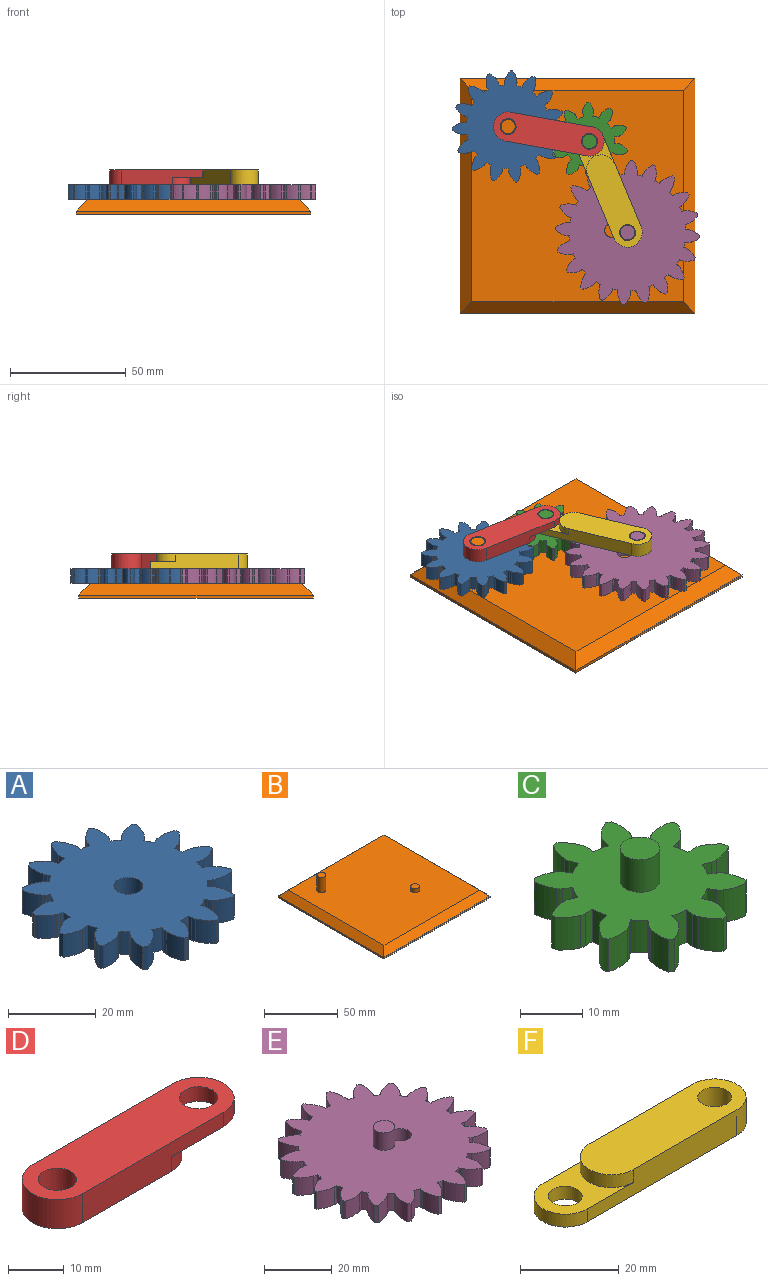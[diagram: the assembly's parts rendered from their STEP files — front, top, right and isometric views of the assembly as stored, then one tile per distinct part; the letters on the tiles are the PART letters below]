
ASSEMBLY  parts=6 mates=6
PART A: 123 faces, bbox 48.3x48.1x6.4 mm
  f0: plane 48.35x48.08mm, normal (0,0,1), area 1375mm2, adj f1,f2,f3,f4,f5,f6,f7,f9
  f1: plane 6.35x0.77mm, normal (-0.96,0.29,0), area 5.1mm2, adj f0,f7,f8,f9
  f2: plane 6.35x0.69mm, normal (0.86,-0.52,0), area 5.1mm2, adj f0,f3,f8,f25
  f3: cylinder r=4.25mm len=6.35mm, axis (0,0,-1), area 6.7mm2, adj f0,f2,f4,f8
  f4: cylinder r=9.71mm len=6.35mm, axis (0,0,-1), area 31.8mm2, adj f0,f3,f5,f8
  f5: plane 6.35x0.91mm, normal (0.41,0.91,0), area 6.3mm2, adj f0,f4,f6,f8
  f6: cylinder r=9.71mm len=6.35mm, axis (0,0,-1), area 31.8mm2, adj f0,f5,f7,f8
  f7: cylinder r=4.25mm len=6.35mm, axis (0,0,-1), area 6.7mm2, adj f0,f1,f6,f8
  f8: plane 48.35x48.08mm, normal (0,0,-1), area 1375mm2, adj f1,f2,f3,f4,f5,f6,f7,f9
  f9: cylinder r=18.11mm len=6.35mm, axis (0,0,-1), area 15.9mm2, adj f0,f1,f8,f117
  f10: plane 6.35x0.8mm, normal (-0.02,1,0), area 5.1mm2, adj f0,f8,f16,f17
  f11: plane 6.35x0.78mm, normal (-0.23,-0.97,0), area 5.1mm2, adj f0,f8,f12,f34
  f12: cylinder r=4.25mm len=6.35mm, axis (0,0,-1), area 6.7mm2, adj f0,f8,f11,f13
  f13: cylinder r=9.71mm len=6.35mm, axis (0,0,-1), area 31.8mm2, adj f0,f8,f12,f14
  f14: plane 6.35x0.99mm, normal (0.99,-0.1,0), area 6.3mm2, adj f0,f8,f13,f15
  f15: cylinder r=9.71mm len=6.35mm, axis (0,0,-1), area 31.8mm2, adj f0,f8,f14,f16
  f16: cylinder r=4.25mm len=6.35mm, axis (0,0,-1), area 6.7mm2, adj f0,f8,f10,f15
  f17: cylinder r=18.11mm len=6.35mm, axis (0,0,-1), area 15.9mm2, adj f0,f8,f10,f27
  f18: plane 6.35x0.61mm, normal (-0.76,0.65,0), area 5.1mm2, adj f0,f8,f24,f25
  f19: plane 6.35x0.66mm, normal (0.57,-0.82,0), area 5.1mm2, adj f0,f8,f20,f33
  f20: cylinder r=4.25mm len=6.35mm, axis (0,0,-1), area 6.7mm2, adj f0,f8,f19,f21
  f21: cylinder r=9.71mm len=6.35mm, axis (0,0,-1), area 31.8mm2, adj f0,f8,f20,f22
  f22: plane 6.35x0.74mm, normal (0.74,0.67,0), area 6.3mm2, adj f0,f8,f21,f23
  f23: cylinder r=9.71mm len=6.35mm, axis (0,0,-1), area 31.8mm2, adj f0,f8,f22,f24
  f24: cylinder r=4.25mm len=6.35mm, axis (0,0,-1), area 6.7mm2, adj f0,f8,f18,f23
  f25: cylinder r=18.11mm len=6.35mm, axis (0,0,-1), area 15.9mm2, adj f0,f2,f8,f18
  f26: plane 6.35x0.73mm, normal (-0.42,0.91,0), area 5.1mm2, adj f0,f8,f32,f33
  f27: plane 6.35x0.79mm, normal (0.19,-0.98,0), area 5.1mm2, adj f0,f8,f17,f28
  f28: cylinder r=4.25mm len=6.35mm, axis (0,0,-1), area 6.7mm2, adj f0,f8,f27,f29
  f29: cylinder r=9.71mm len=6.35mm, axis (0,0,-1), area 31.8mm2, adj f0,f8,f28,f30
  f30: plane 6.35x0.95mm, normal (0.95,0.31,0), area 6.3mm2, adj f0,f8,f29,f31
  f31: cylinder r=9.71mm len=6.35mm, axis (0,0,-1), area 31.8mm2, adj f0,f8,f30,f32
  f32: cylinder r=4.25mm len=6.35mm, axis (0,0,-1), area 6.7mm2, adj f0,f8,f26,f31
  f33: cylinder r=18.11mm len=6.35mm, axis (0,0,-1), area 15.9mm2, adj f0,f8,f19,f26
  f34: cylinder r=18.11mm len=6.35mm, axis (0,0,-1), area 15.9mm2, adj f0,f8,f11,f95
  f35: cylinder r=18.11mm len=6.35mm, axis (0,0,-1), area 15.9mm2, adj f0,f8,f110,f116
  f36: cylinder r=18.11mm len=6.35mm, axis (0,0,-1), area 15.9mm2, adj f0,f8,f103,f109
  f37: cylinder r=18.11mm len=6.35mm, axis (0,0,-1), area 15.9mm2, adj f0,f8,f88,f96
  f38: cylinder r=18.11mm len=6.35mm, axis (0,0,-1), area 15.9mm2, adj f0,f8,f81,f89
  f39: cylinder r=18.11mm len=6.35mm, axis (0,0,-1), area 15.9mm2, adj f0,f8,f74,f82
  f40: cylinder r=18.11mm len=6.35mm, axis (0,0,-1), area 15.9mm2, adj f0,f8,f67,f75
  f41: cylinder r=18.11mm len=6.35mm, axis (0,0,-1), area 15.9mm2, adj f0,f8,f60,f68
  f42: cylinder r=18.11mm len=6.35mm, axis (0,0,-1), area 15.9mm2, adj f0,f8,f53,f61
  f43: cylinder r=18.11mm len=6.35mm, axis (0,0,-1), area 15.9mm2, adj f0,f8,f46,f54
  f44: cylinder r=18.11mm len=6.35mm, axis (0,0,-1), area 15.9mm2, adj f0,f8,f47,f102
  f45: cylinder r=3.3mm len=6.6mm, axis (0,0,-1), area 131.7mm2, adj f0,f8
  f46: plane 6.35x0.79mm, normal (-0.19,-0.98,0), area 5.1mm2, adj f0,f8,f43,f52
  f47: plane 6.35x0.73mm, normal (0.42,0.91,0), area 5.1mm2, adj f0,f8,f44,f48
  f48: cylinder r=4.25mm len=6.35mm, axis (0,0,-1), area 6.7mm2, adj f0,f8,f47,f49
  f49: cylinder r=9.71mm len=6.35mm, axis (0,0,-1), area 31.8mm2, adj f0,f8,f48,f50
  f50: plane 6.35x0.95mm, normal (-0.95,0.31,0), area 6.3mm2, adj f0,f8,f49,f51
  f51: cylinder r=9.71mm len=6.35mm, axis (0,0,-1), area 31.8mm2, adj f0,f8,f50,f52
  f52: cylinder r=4.25mm len=6.35mm, axis (0,0,-1), area 6.7mm2, adj f0,f8,f46,f51
  f53: plane 6.35x0.78mm, normal (0.23,-0.97,0), area 5.1mm2, adj f0,f8,f42,f59
  f54: plane 6.35x0.8mm, normal (0.02,1,0), area 5.1mm2, adj f0,f8,f43,f55
  f55: cylinder r=4.25mm len=6.35mm, axis (0,0,-1), area 6.7mm2, adj f0,f8,f54,f56
  f56: cylinder r=9.71mm len=6.35mm, axis (0,0,-1), area 31.8mm2, adj f0,f8,f55,f57
  f57: plane 6.35x0.99mm, normal (-0.99,-0.1,0), area 6.3mm2, adj f0,f8,f56,f58
  f58: cylinder r=9.71mm len=6.35mm, axis (0,0,-1), area 31.8mm2, adj f0,f8,f57,f59
  f59: cylinder r=4.25mm len=6.35mm, axis (0,0,-1), area 6.7mm2, adj f0,f8,f53,f58
  f60: plane 6.35x0.64mm, normal (0.6,-0.8,0), area 5.1mm2, adj f0,f8,f41,f66
  f61: plane 6.35x0.74mm, normal (-0.39,0.92,0), area 5.1mm2, adj f0,f8,f42,f62
  f62: cylinder r=4.25mm len=6.35mm, axis (0,0,-1), area 6.7mm2, adj f0,f8,f61,f63
  f63: cylinder r=9.71mm len=6.35mm, axis (0,0,-1), area 31.8mm2, adj f0,f8,f62,f64
  f64: plane 6.35x0.87mm, normal (-0.87,-0.5,0), area 6.3mm2, adj f0,f8,f63,f65
  f65: cylinder r=9.71mm len=6.35mm, axis (0,0,-1), area 31.8mm2, adj f0,f8,f64,f66
  f66: cylinder r=4.25mm len=6.35mm, axis (0,0,-1), area 6.7mm2, adj f0,f8,f60,f65
  f67: plane 6.35x0.71mm, normal (0.88,-0.48,0), area 5.1mm2, adj f0,f8,f40,f73
  f68: plane 6.35x0.59mm, normal (-0.73,0.68,0), area 5.1mm2, adj f0,f8,f41,f69
  f69: cylinder r=4.25mm len=6.35mm, axis (0,0,-1), area 6.7mm2, adj f0,f8,f68,f70
  f70: cylinder r=9.71mm len=6.35mm, axis (0,0,-1), area 31.8mm2, adj f0,f8,f69,f71
  f71: plane 6.35x0.81mm, normal (-0.59,-0.81,0), area 6.3mm2, adj f0,f8,f70,f72
  f72: cylinder r=9.71mm len=6.35mm, axis (0,0,-1), area 31.8mm2, adj f0,f8,f71,f73
  f73: cylinder r=4.25mm len=6.35mm, axis (0,0,-1), area 6.7mm2, adj f0,f8,f67,f72
  f74: plane 6.35x0.8mm, normal (1,-0.09,0), area 5.1mm2, adj f0,f8,f39,f80
  f75: plane 6.35x0.76mm, normal (-0.94,0.33,0), area 5.1mm2, adj f0,f8,f40,f76
  f76: cylinder r=4.25mm len=6.35mm, axis (0,0,-1), area 6.7mm2, adj f0,f8,f75,f77
  f77: cylinder r=9.71mm len=6.35mm, axis (0,0,-1), area 31.8mm2, adj f0,f8,f76,f78
  f78: plane 6.35x0.98mm, normal (-0.21,-0.98,0), area 6.3mm2, adj f0,f8,f77,f79
  f79: cylinder r=9.71mm len=6.35mm, axis (0,0,-1), area 31.8mm2, adj f0,f8,f78,f80
  f80: cylinder r=4.25mm len=6.35mm, axis (0,0,-1), area 6.7mm2, adj f0,f8,f74,f79
  f81: plane 6.35x0.76mm, normal (0.94,0.33,0), area 5.1mm2, adj f0,f8,f38,f87
  f82: plane 6.35x0.8mm, normal (-1,-0.09,0), area 5.1mm2, adj f0,f8,f39,f83
  f83: cylinder r=4.25mm len=6.35mm, axis (0,0,-1), area 6.7mm2, adj f0,f8,f82,f84
  f84: cylinder r=9.71mm len=6.35mm, axis (0,0,-1), area 31.8mm2, adj f0,f8,f83,f85
  f85: plane 6.35x0.98mm, normal (0.21,-0.98,0), area 6.3mm2, adj f0,f8,f84,f86
  f86: cylinder r=9.71mm len=6.35mm, axis (0,0,-1), area 31.8mm2, adj f0,f8,f85,f87
  f87: cylinder r=4.25mm len=6.35mm, axis (0,0,-1), area 6.7mm2, adj f0,f8,f81,f86
  f88: plane 6.35x0.59mm, normal (0.73,0.68,0), area 5.1mm2, adj f0,f8,f37,f94
  f89: plane 6.35x0.71mm, normal (-0.88,-0.48,0), area 5.1mm2, adj f0,f8,f38,f90
  f90: cylinder r=4.25mm len=6.35mm, axis (0,0,-1), area 6.7mm2, adj f0,f8,f89,f91
  f91: cylinder r=9.71mm len=6.35mm, axis (0,0,-1), area 31.8mm2, adj f0,f8,f90,f92
  f92: plane 6.35x0.81mm, normal (0.59,-0.81,0), area 6.3mm2, adj f0,f8,f91,f93
  f93: cylinder r=9.71mm len=6.35mm, axis (0,0,-1), area 31.8mm2, adj f0,f8,f92,f94
  f94: cylinder r=4.25mm len=6.35mm, axis (0,0,-1), area 6.7mm2, adj f0,f8,f88,f93
  f95: plane 6.35x0.74mm, normal (0.39,0.92,0), area 5.1mm2, adj f0,f8,f34,f101
  f96: plane 6.35x0.64mm, normal (-0.6,-0.8,0), area 5.1mm2, adj f0,f8,f37,f97
  f97: cylinder r=4.25mm len=6.35mm, axis (0,0,-1), area 6.7mm2, adj f0,f8,f96,f98
  f98: cylinder r=9.71mm len=6.35mm, axis (0,0,-1), area 31.8mm2, adj f0,f8,f97,f99
  f99: plane 6.35x0.87mm, normal (0.87,-0.5,0), area 6.3mm2, adj f0,f8,f98,f100
  f100: cylinder r=9.71mm len=6.35mm, axis (0,0,-1), area 31.8mm2, adj f0,f8,f99,f101
  f101: cylinder r=4.25mm len=6.35mm, axis (0,0,-1), area 6.7mm2, adj f0,f8,f95,f100
  f102: plane 6.35x0.66mm, normal (-0.57,-0.82,0), area 5.1mm2, adj f0,f8,f44,f108
  f103: plane 6.35x0.61mm, normal (0.76,0.65,0), area 5.1mm2, adj f0,f8,f36,f104
  f104: cylinder r=4.25mm len=6.35mm, axis (0,0,-1), area 6.7mm2, adj f0,f8,f103,f105
  f105: cylinder r=9.71mm len=6.35mm, axis (0,0,-1), area 31.8mm2, adj f0,f8,f104,f106
  f106: plane 6.35x0.74mm, normal (-0.74,0.67,0), area 6.3mm2, adj f0,f8,f105,f107
  f107: cylinder r=9.71mm len=6.35mm, axis (0,0,-1), area 31.8mm2, adj f0,f8,f106,f108
  f108: cylinder r=4.25mm len=6.35mm, axis (0,0,-1), area 6.7mm2, adj f0,f8,f102,f107
  f109: plane 6.35x0.69mm, normal (-0.86,-0.52,0), area 5.1mm2, adj f0,f8,f36,f115
  f110: plane 6.35x0.77mm, normal (0.96,0.29,0), area 5.1mm2, adj f0,f8,f35,f111
  f111: cylinder r=4.25mm len=6.35mm, axis (0,0,-1), area 6.7mm2, adj f0,f8,f110,f112
  f112: cylinder r=9.71mm len=6.35mm, axis (0,0,-1), area 31.8mm2, adj f0,f8,f111,f113
  f113: plane 6.35x0.91mm, normal (-0.41,0.91,0), area 6.3mm2, adj f0,f8,f112,f114
  f114: cylinder r=9.71mm len=6.35mm, axis (0,0,-1), area 31.8mm2, adj f0,f8,f113,f115
  f115: cylinder r=4.25mm len=6.35mm, axis (0,0,-1), area 6.7mm2, adj f0,f8,f109,f114
  f116: plane 6.35x0.8mm, normal (-0.99,-0.12,0), area 5.1mm2, adj f0,f8,f35,f122
  f117: plane 6.35x0.8mm, normal (0.99,-0.12,0), area 5.1mm2, adj f0,f8,f9,f118
  f118: cylinder r=4.25mm len=6.35mm, axis (0,0,-1), area 6.7mm2, adj f0,f8,f117,f119
  f119: cylinder r=9.71mm len=6.35mm, axis (0,0,-1), area 31.8mm2, adj f0,f8,f118,f120
  f120: plane 6.35x1mm, normal (0,1,0), area 6.3mm2, adj f0,f8,f119,f121
  f121: cylinder r=9.71mm len=6.35mm, axis (0,0,-1), area 31.8mm2, adj f0,f8,f120,f122
  f122: cylinder r=4.25mm len=6.35mm, axis (0,0,-1), area 6.7mm2, adj f0,f8,f116,f121
PART B: 14 faces, bbox 101.6x101.6x19.1 mm
  f0: plane 101.6x1.27mm, normal (0,1,0), area 129mm2, adj f1,f3,f4,f9
  f1: plane 101.6x1.27mm, normal (-1,0,0), area 129mm2, adj f0,f2,f4,f8
  f2: plane 101.6x1.27mm, normal (0,-1,0), area 129mm2, adj f1,f3,f4,f10
  f3: plane 101.6x1.27mm, normal (1,0,0), area 129mm2, adj f0,f2,f4,f11
  f4: plane 101.6x101.6mm, normal (0,0,-1), area 10322.6mm2, adj f0,f1,f2,f3
  f5: plane 91.44x91.44mm, normal (0,0,1), area 8302.9mm2, adj f6,f8,f9,f10,f11,f12
  f6: cylinder r=3.05mm len=6.1mm, axis (0,0,-1), area 60.8mm2, adj f5,f7
  f7: plane 6.1x6.1mm, normal (0,0,1), area 29.2mm2, adj f6
  f8: plane 101.6x5.08mm, normal (-0.71,0,0.71), area 693.4mm2, adj f1,f5,f9,f10
  f9: plane 101.6x5.08mm, normal (0,0.71,0.71), area 693.4mm2, adj f0,f5,f8,f11
  f10: plane 101.6x5.08mm, normal (0,-0.71,0.71), area 693.4mm2, adj f2,f5,f8,f11
  f11: plane 101.6x5.08mm, normal (0.71,0,0.71), area 693.4mm2, adj f3,f5,f9,f10
  f12: cylinder r=3.05mm len=12.7mm, axis (0,0,-1), area 243.2mm2, adj f5,f13
  f13: plane 6.1x6.1mm, normal (0,0,1), area 29.2mm2, adj f12
PART C: 84 faces, bbox 33.6x33.7x12.7 mm
  f0: plane 33.74x33.62mm, normal (0,0,1), area 573.8mm2, adj f1,f2,f3,f4,f6,f7,f8,f9
  f1: cylinder r=2.25mm len=6.35mm, axis (0,0,-1), area 6.5mm2, adj f0,f2,f5,f7
  f2: plane 6.35x1.56mm, normal (0.96,-0.27,0), area 10.3mm2, adj f0,f1,f5,f9
  f3: plane 6.35x1.24mm, normal (-0.77,0.64,0), area 10.3mm2, adj f0,f4,f5,f17
  f4: cylinder r=2.25mm len=6.35mm, axis (0,0,-1), area 6.5mm2, adj f0,f3,f5,f6
  f5: plane 33.74x33.62mm, normal (0,0,-1), area 605.5mm2, adj f1,f2,f3,f4,f6,f7,f8,f9
  f6: cylinder r=8.54mm len=6.35mm, axis (0,0,-1), area 26mm2, adj f0,f4,f5,f8
  f7: cylinder r=8.54mm len=6.35mm, axis (0,0,-1), area 26mm2, adj f0,f1,f5,f8
  f8: plane 6.35x0.87mm, normal (-0.47,-0.88,0), area 6.3mm2, adj f0,f5,f6,f7
  f9: cylinder r=10.96mm len=6.35mm, axis (0,0,-1), area 18mm2, adj f0,f2,f5,f76
  f10: cylinder r=2.25mm len=6.35mm, axis (0,0,-1), area 6.5mm2, adj f0,f5,f11,f15
  f11: plane 6.35x1.26mm, normal (0.62,-0.78,0), area 10.3mm2, adj f0,f5,f10,f17
  f12: plane 6.35x1.57mm, normal (-0.24,0.97,0), area 10.3mm2, adj f0,f5,f13,f25
  f13: cylinder r=2.25mm len=6.35mm, axis (0,0,-1), area 6.5mm2, adj f0,f5,f12,f14
  f14: cylinder r=8.54mm len=6.35mm, axis (0,0,-1), area 26mm2, adj f0,f5,f13,f16
  f15: cylinder r=8.54mm len=6.35mm, axis (0,0,-1), area 26mm2, adj f0,f5,f10,f16
  f16: plane 6.35x0.89mm, normal (-0.9,-0.44,0), area 6.3mm2, adj f0,f5,f14,f15
  f17: cylinder r=10.96mm len=6.35mm, axis (0,0,-1), area 18mm2, adj f0,f3,f5,f11
  f18: cylinder r=2.25mm len=6.35mm, axis (0,0,-1), area 6.5mm2, adj f0,f5,f19,f23
  f19: plane 6.35x1.62mm, normal (0.04,-1,0), area 10.3mm2, adj f0,f5,f18,f25
  f20: plane 6.35x1.5mm, normal (0.38,0.93,0), area 10.3mm2, adj f0,f5,f21,f33
  f21: cylinder r=2.25mm len=6.35mm, axis (0,0,-1), area 6.5mm2, adj f0,f5,f20,f22
  f22: cylinder r=8.54mm len=6.35mm, axis (0,0,-1), area 26mm2, adj f0,f5,f21,f24
  f23: cylinder r=8.54mm len=6.35mm, axis (0,0,-1), area 26mm2, adj f0,f5,f18,f24
  f24: plane 6.35x0.97mm, normal (-0.99,0.17,0), area 6.3mm2, adj f0,f5,f22,f23
  f25: cylinder r=10.96mm len=6.35mm, axis (0,0,-1), area 18mm2, adj f0,f5,f12,f19
  f26: cylinder r=2.25mm len=6.35mm, axis (0,0,-1), area 6.5mm2, adj f0,f5,f27,f31
  f27: plane 6.35x1.35mm, normal (-0.55,-0.83,0), area 10.3mm2, adj f0,f5,f26,f33
  f28: plane 6.35x1.37mm, normal (0.85,0.53,0), area 10.3mm2, adj f0,f5,f29,f41
  f29: cylinder r=2.25mm len=6.35mm, axis (0,0,-1), area 6.5mm2, adj f0,f5,f28,f30
  f30: cylinder r=8.54mm len=6.35mm, axis (0,0,-1), area 26mm2, adj f0,f5,f29,f32
  f31: cylinder r=8.54mm len=6.35mm, axis (0,0,-1), area 26mm2, adj f0,f5,f26,f32
  f32: plane 6.35x0.71mm, normal (-0.7,0.72,0), area 6.3mm2, adj f0,f5,f30,f31
  f33: cylinder r=10.96mm len=6.35mm, axis (0,0,-1), area 18mm2, adj f0,f5,f20,f27
  f34: cylinder r=2.25mm len=6.35mm, axis (0,0,-1), area 6.5mm2, adj f0,f5,f35,f39
  f35: plane 6.35x1.51mm, normal (-0.94,-0.35,0), area 10.3mm2, adj f0,f5,f34,f41
  f36: plane 6.35x1.61mm, normal (1,-0.07,0), area 10.3mm2, adj f0,f5,f37,f49
  f37: cylinder r=2.25mm len=6.35mm, axis (0,0,-1), area 6.5mm2, adj f0,f5,f36,f38
  f38: cylinder r=8.54mm len=6.35mm, axis (0,0,-1), area 26mm2, adj f0,f5,f37,f40
  f39: cylinder r=8.54mm len=6.35mm, axis (0,0,-1), area 26mm2, adj f0,f5,f34,f40
  f40: plane 6.35x0.98mm, normal (-0.14,0.99,0), area 6.3mm2, adj f0,f5,f38,f39
  f41: cylinder r=10.96mm len=6.35mm, axis (0,0,-1), area 18mm2, adj f0,f5,f28,f35
  f42: cylinder r=2.25mm len=6.35mm, axis (0,0,-1), area 6.5mm2, adj f0,f5,f43,f47
  f43: plane 6.35x1.56mm, normal (-0.96,0.27,0), area 10.3mm2, adj f0,f5,f42,f49
  f44: plane 6.35x1.24mm, normal (0.77,-0.64,0), area 10.3mm2, adj f0,f5,f45,f57
  f45: cylinder r=2.25mm len=6.35mm, axis (0,0,-1), area 6.5mm2, adj f0,f5,f44,f46
  f46: cylinder r=8.54mm len=6.35mm, axis (0,0,-1), area 26mm2, adj f0,f5,f45,f48
  f47: cylinder r=8.54mm len=6.35mm, axis (0,0,-1), area 26mm2, adj f0,f5,f42,f48
  f48: plane 6.35x0.87mm, normal (0.47,0.88,0), area 6.3mm2, adj f0,f5,f46,f47
  f49: cylinder r=10.96mm len=6.35mm, axis (0,0,-1), area 18mm2, adj f0,f5,f36,f43
  f50: cylinder r=2.25mm len=6.35mm, axis (0,0,-1), area 6.5mm2, adj f0,f5,f51,f55
  f51: plane 6.35x1.26mm, normal (-0.62,0.78,0), area 10.3mm2, adj f0,f5,f50,f57
  f52: plane 6.35x1.57mm, normal (0.24,-0.97,0), area 10.3mm2, adj f0,f5,f53,f65
  f53: cylinder r=2.25mm len=6.35mm, axis (0,0,-1), area 6.5mm2, adj f0,f5,f52,f54
  f54: cylinder r=8.54mm len=6.35mm, axis (0,0,-1), area 26mm2, adj f0,f5,f53,f56
  f55: cylinder r=8.54mm len=6.35mm, axis (0,0,-1), area 26mm2, adj f0,f5,f50,f56
  f56: plane 6.35x0.89mm, normal (0.9,0.44,0), area 6.3mm2, adj f0,f5,f54,f55
  f57: cylinder r=10.96mm len=6.35mm, axis (0,0,-1), area 18mm2, adj f0,f5,f44,f51
  f58: cylinder r=2.25mm len=6.35mm, axis (0,0,-1), area 6.5mm2, adj f0,f5,f59,f63
  f59: plane 6.35x1.62mm, normal (-0.04,1,0), area 10.3mm2, adj f0,f5,f58,f65
  f60: plane 6.35x1.5mm, normal (-0.38,-0.93,0), area 10.3mm2, adj f0,f5,f61,f73
  f61: cylinder r=2.25mm len=6.35mm, axis (0,0,-1), area 6.5mm2, adj f0,f5,f60,f62
  f62: cylinder r=8.54mm len=6.35mm, axis (0,0,-1), area 26mm2, adj f0,f5,f61,f64
  f63: cylinder r=8.54mm len=6.35mm, axis (0,0,-1), area 26mm2, adj f0,f5,f58,f64
  f64: plane 6.35x0.97mm, normal (0.99,-0.17,0), area 6.3mm2, adj f0,f5,f62,f63
  f65: cylinder r=10.96mm len=6.35mm, axis (0,0,-1), area 18mm2, adj f0,f5,f52,f59
  f66: cylinder r=2.25mm len=6.35mm, axis (0,0,-1), area 6.5mm2, adj f0,f5,f67,f71
  f67: plane 6.35x1.35mm, normal (0.55,0.83,0), area 10.3mm2, adj f0,f5,f66,f73
  f68: plane 6.35x1.37mm, normal (-0.85,-0.53,0), area 10.3mm2, adj f0,f5,f69,f81
  f69: cylinder r=2.25mm len=6.35mm, axis (0,0,-1), area 6.5mm2, adj f0,f5,f68,f70
  f70: cylinder r=8.54mm len=6.35mm, axis (0,0,-1), area 26mm2, adj f0,f5,f69,f72
  f71: cylinder r=8.54mm len=6.35mm, axis (0,0,-1), area 26mm2, adj f0,f5,f66,f72
  f72: plane 6.35x0.71mm, normal (0.7,-0.72,0), area 6.3mm2, adj f0,f5,f70,f71
  f73: cylinder r=10.96mm len=6.35mm, axis (0,0,-1), area 18mm2, adj f0,f5,f60,f67
  f74: cylinder r=2.25mm len=6.35mm, axis (0,0,-1), area 6.5mm2, adj f0,f5,f75,f79
  f75: plane 6.35x1.51mm, normal (0.94,0.35,0), area 10.3mm2, adj f0,f5,f74,f81
  f76: plane 6.35x1.61mm, normal (-1,0.07,0), area 10.3mm2, adj f0,f5,f9,f77
  f77: cylinder r=2.25mm len=6.35mm, axis (0,0,-1), area 6.5mm2, adj f0,f5,f76,f78
  f78: cylinder r=8.54mm len=6.35mm, axis (0,0,-1), area 26mm2, adj f0,f5,f77,f80
  f79: cylinder r=8.54mm len=6.35mm, axis (0,0,-1), area 26mm2, adj f0,f5,f74,f80
  f80: plane 6.35x0.98mm, normal (0.14,-0.99,0), area 6.3mm2, adj f0,f5,f78,f79
  f81: cylinder r=10.96mm len=6.35mm, axis (0,0,-1), area 18mm2, adj f0,f5,f68,f75
  f82: cylinder r=3.17mm len=6.35mm, axis (0,0,-1), area 126.7mm2, adj f0,f83
  f83: plane 6.35x6.35mm, normal (0,0,1), area 31.7mm2, adj f82
PART D: 10 faces, bbox 48.5x12.7x6.4 mm
  f0: plane 35.76x6.35mm, normal (0,-1,0), area 185.2mm2, adj f1,f3,f6,f7,f8,f9
  f1: cylinder r=6.35mm len=12.7mm, axis (0,0,-1), area 63.3mm2, adj f0,f2,f6,f7
  f2: plane 35.76x6.35mm, normal (0,1,0), area 185.2mm2, adj f1,f3,f6,f7,f8,f9
  f3: cylinder r=6.35mm len=12.7mm, axis (0,0,-1), area 126.7mm2, adj f0,f2,f6,f9
  f4: cylinder r=3.43mm len=6.86mm, axis (0,0,-1), area 136.8mm2, adj f6,f9
  f5: cylinder r=3.43mm len=6.86mm, axis (0,0,-1), area 68.4mm2, adj f6,f7
  f6: plane 48.46x12.7mm, normal (0,0,1), area 507mm2, adj f0,f1,f2,f3,f4,f5
  f7: plane 19.56x12.7mm, normal (0,0,-1), area 130.8mm2, adj f0,f1,f2,f5,f8
  f8: cylinder r=6.35mm len=12.7mm, axis (0,0,1), area 63.3mm2, adj f0,f2,f7,f9
  f9: plane 35.26x12.7mm, normal (0,0,-1), area 376.2mm2, adj f0,f2,f3,f4,f8
PART E: 125 faces, bbox 62.5x62.5x12.7 mm
  f0: plane 62.47x62.47mm, normal (0,0,1), area 2455.4mm2, adj f1,f2,f3,f4,f5,f7,f8,f9
  f1: plane 6.35x0.99mm, normal (0.08,-1,0), area 6.3mm2, adj f0,f2,f5,f6
  f2: cylinder r=10.8mm len=6.35mm, axis (0,0,-1), area 36.8mm2, adj f0,f1,f3,f6
  f3: cylinder r=3.57mm len=6.35mm, axis (0,0,-1), area 6.8mm2, adj f0,f2,f6,f7
  f4: cylinder r=3.57mm len=6.35mm, axis (0,0,-1), area 6.8mm2, adj f0,f5,f6,f70
  f5: cylinder r=10.8mm len=6.35mm, axis (0,0,-1), area 36.8mm2, adj f0,f1,f4,f6
  f6: plane 62.47x62.47mm, normal (0,0,-1), area 2487mm2, adj f1,f2,f3,f4,f5,f7,f8,f9
  f7: cylinder r=25.2mm len=6.35mm, axis (0,0,-1), area 13.3mm2, adj f0,f3,f6,f23
  f8: plane 6.35x0.85mm, normal (0.86,-0.52,0), area 6.3mm2, adj f0,f6,f9,f12
  f9: cylinder r=10.8mm len=6.35mm, axis (0,0,-1), area 36.8mm2, adj f0,f6,f8,f10
  f10: cylinder r=3.57mm len=6.35mm, axis (0,0,-1), area 6.8mm2, adj f0,f6,f9,f13
  f11: cylinder r=3.57mm len=6.35mm, axis (0,0,-1), area 6.8mm2, adj f0,f6,f12,f19
  f12: cylinder r=10.8mm len=6.35mm, axis (0,0,-1), area 36.8mm2, adj f0,f6,f8,f11
  f13: cylinder r=25.2mm len=6.35mm, axis (0,0,-1), area 13.3mm2, adj f0,f6,f10,f29
  f14: plane 6.35x0.75mm, normal (0.65,-0.76,0), area 6.3mm2, adj f0,f6,f15,f18
  f15: cylinder r=10.8mm len=6.35mm, axis (0,0,-1), area 36.8mm2, adj f0,f6,f14,f16
  f16: cylinder r=3.57mm len=6.35mm, axis (0,0,-1), area 6.8mm2, adj f0,f6,f15,f19
  f17: cylinder r=3.57mm len=6.35mm, axis (0,0,-1), area 6.8mm2, adj f0,f6,f18,f25
  f18: cylinder r=10.8mm len=6.35mm, axis (0,0,-1), area 36.8mm2, adj f0,f6,f14,f17
  f19: cylinder r=25.2mm len=6.35mm, axis (0,0,-1), area 13.3mm2, adj f0,f6,f11,f16
  f20: plane 6.35x0.92mm, normal (0.39,-0.92,0), area 6.3mm2, adj f0,f6,f21,f24
  f21: cylinder r=10.8mm len=6.35mm, axis (0,0,-1), area 36.8mm2, adj f0,f6,f20,f22
  f22: cylinder r=3.57mm len=6.35mm, axis (0,0,-1), area 6.8mm2, adj f0,f6,f21,f25
  f23: cylinder r=3.57mm len=6.35mm, axis (0,0,-1), area 6.8mm2, adj f0,f6,f7,f24
  f24: cylinder r=10.8mm len=6.35mm, axis (0,0,-1), area 36.8mm2, adj f0,f6,f20,f23
  f25: cylinder r=25.2mm len=6.35mm, axis (0,0,-1), area 13.3mm2, adj f0,f6,f17,f22
  f26: plane 6.35x0.97mm, normal (0.97,-0.23,0), area 6.3mm2, adj f0,f6,f27,f30
  f27: cylinder r=10.8mm len=6.35mm, axis (0,0,-1), area 36.8mm2, adj f0,f6,f26,f28
  f28: cylinder r=3.57mm len=6.35mm, axis (0,0,-1), area 6.8mm2, adj f0,f6,f27,f31
  f29: cylinder r=3.57mm len=6.35mm, axis (0,0,-1), area 6.8mm2, adj f0,f6,f13,f30
  f30: cylinder r=10.8mm len=6.35mm, axis (0,0,-1), area 36.8mm2, adj f0,f6,f26,f29
  f31: cylinder r=25.2mm len=6.35mm, axis (0,0,-1), area 13.3mm2, adj f0,f6,f28,f35
  f32: plane 6.35x0.99mm, normal (1,0.08,0), area 6.3mm2, adj f0,f6,f33,f36
  f33: cylinder r=10.8mm len=6.35mm, axis (0,0,-1), area 36.8mm2, adj f0,f6,f32,f34
  f34: cylinder r=3.57mm len=6.35mm, axis (0,0,-1), area 6.8mm2, adj f0,f6,f33,f37
  f35: cylinder r=3.57mm len=6.35mm, axis (0,0,-1), area 6.8mm2, adj f0,f6,f31,f36
  f36: cylinder r=10.8mm len=6.35mm, axis (0,0,-1), area 36.8mm2, adj f0,f6,f32,f35
  f37: cylinder r=25.2mm len=6.35mm, axis (0,0,-1), area 13.3mm2, adj f0,f6,f34,f41
  f38: plane 6.35x0.92mm, normal (0.92,0.39,0), area 6.3mm2, adj f0,f6,f39,f42
  f39: cylinder r=10.8mm len=6.35mm, axis (0,0,-1), area 36.8mm2, adj f0,f6,f38,f40
  f40: cylinder r=3.57mm len=6.35mm, axis (0,0,-1), area 6.8mm2, adj f0,f6,f39,f43
  f41: cylinder r=3.57mm len=6.35mm, axis (0,0,-1), area 6.8mm2, adj f0,f6,f37,f42
  f42: cylinder r=10.8mm len=6.35mm, axis (0,0,-1), area 36.8mm2, adj f0,f6,f38,f41
  f43: cylinder r=25.2mm len=6.35mm, axis (0,0,-1), area 13.3mm2, adj f0,f6,f40,f47
  f44: plane 6.35x0.75mm, normal (0.76,0.65,0), area 6.3mm2, adj f0,f6,f45,f48
  f45: cylinder r=10.8mm len=6.35mm, axis (0,0,-1), area 36.8mm2, adj f0,f6,f44,f46
  f46: cylinder r=3.57mm len=6.35mm, axis (0,0,-1), area 6.8mm2, adj f0,f6,f45,f49
  f47: cylinder r=3.57mm len=6.35mm, axis (0,0,-1), area 6.8mm2, adj f0,f6,f43,f48
  f48: cylinder r=10.8mm len=6.35mm, axis (0,0,-1), area 36.8mm2, adj f0,f6,f44,f47
  f49: cylinder r=25.2mm len=6.35mm, axis (0,0,-1), area 13.3mm2, adj f0,f6,f46,f53
  f50: plane 6.35x0.85mm, normal (0.52,0.86,0), area 6.3mm2, adj f0,f6,f51,f54
  f51: cylinder r=10.8mm len=6.35mm, axis (0,0,-1), area 36.8mm2, adj f0,f6,f50,f52
  f52: cylinder r=3.57mm len=6.35mm, axis (0,0,-1), area 6.8mm2, adj f0,f6,f51,f55
  f53: cylinder r=3.57mm len=6.35mm, axis (0,0,-1), area 6.8mm2, adj f0,f6,f49,f54
  f54: cylinder r=10.8mm len=6.35mm, axis (0,0,-1), area 36.8mm2, adj f0,f6,f50,f53
  f55: cylinder r=25.2mm len=6.35mm, axis (0,0,-1), area 13.3mm2, adj f0,f6,f52,f59
  f56: plane 6.35x0.97mm, normal (0.23,0.97,0), area 6.3mm2, adj f0,f6,f57,f60
  f57: cylinder r=10.8mm len=6.35mm, axis (0,0,-1), area 36.8mm2, adj f0,f6,f56,f58
  f58: cylinder r=3.57mm len=6.35mm, axis (0,0,-1), area 6.8mm2, adj f0,f6,f57,f61
  f59: cylinder r=3.57mm len=6.35mm, axis (0,0,-1), area 6.8mm2, adj f0,f6,f55,f60
  f60: cylinder r=10.8mm len=6.35mm, axis (0,0,-1), area 36.8mm2, adj f0,f6,f56,f59
  f61: cylinder r=25.2mm len=6.35mm, axis (0,0,-1), area 13.3mm2, adj f0,f6,f58,f80
  f62: cylinder r=25.2mm len=6.35mm, axis (0,0,-1), area 13.3mm2, adj f0,f6,f79,f120
  f63: cylinder r=25.2mm len=6.35mm, axis (0,0,-1), area 13.3mm2, adj f0,f6,f115,f119
  f64: cylinder r=25.2mm len=6.35mm, axis (0,0,-1), area 13.3mm2, adj f0,f6,f110,f114
  f65: cylinder r=25.2mm len=6.35mm, axis (0,0,-1), area 13.3mm2, adj f0,f6,f105,f109
  f66: cylinder r=25.2mm len=6.35mm, axis (0,0,-1), area 13.3mm2, adj f0,f6,f100,f104
  f67: cylinder r=25.2mm len=6.35mm, axis (0,0,-1), area 13.3mm2, adj f0,f6,f95,f99
  f68: cylinder r=25.2mm len=6.35mm, axis (0,0,-1), area 13.3mm2, adj f0,f6,f90,f94
  f69: cylinder r=25.2mm len=6.35mm, axis (0,0,-1), area 13.3mm2, adj f0,f6,f74,f85
  f70: cylinder r=25.2mm len=6.35mm, axis (0,0,-1), area 13.3mm2, adj f0,f4,f6,f84
  f71: cylinder r=25.2mm len=6.35mm, axis (0,0,-1), area 13.3mm2, adj f0,f6,f75,f89
  f72: plane 6.35x0.85mm, normal (-0.52,-0.86,0), area 6.3mm2, adj f0,f6,f73,f76
  f73: cylinder r=10.8mm len=6.35mm, axis (0,0,-1), area 36.8mm2, adj f0,f6,f72,f74
  f74: cylinder r=3.57mm len=6.35mm, axis (0,0,-1), area 6.8mm2, adj f0,f6,f69,f73
  f75: cylinder r=3.57mm len=6.35mm, axis (0,0,-1), area 6.8mm2, adj f0,f6,f71,f76
  f76: cylinder r=10.8mm len=6.35mm, axis (0,0,-1), area 36.8mm2, adj f0,f6,f72,f75
  f77: plane 6.35x0.99mm, normal (-0.08,1,0), area 6.3mm2, adj f0,f6,f78,f81
  f78: cylinder r=10.8mm len=6.35mm, axis (0,0,-1), area 36.8mm2, adj f0,f6,f77,f79
  f79: cylinder r=3.57mm len=6.35mm, axis (0,0,-1), area 6.8mm2, adj f0,f6,f62,f78
  f80: cylinder r=3.57mm len=6.35mm, axis (0,0,-1), area 6.8mm2, adj f0,f6,f61,f81
  f81: cylinder r=10.8mm len=6.35mm, axis (0,0,-1), area 36.8mm2, adj f0,f6,f77,f80
  f82: plane 6.35x0.97mm, normal (-0.23,-0.97,0), area 6.3mm2, adj f0,f6,f83,f86
  f83: cylinder r=10.8mm len=6.35mm, axis (0,0,-1), area 36.8mm2, adj f0,f6,f82,f84
  f84: cylinder r=3.57mm len=6.35mm, axis (0,0,-1), area 6.8mm2, adj f0,f6,f70,f83
  f85: cylinder r=3.57mm len=6.35mm, axis (0,0,-1), area 6.8mm2, adj f0,f6,f69,f86
  f86: cylinder r=10.8mm len=6.35mm, axis (0,0,-1), area 36.8mm2, adj f0,f6,f82,f85
  f87: plane 6.35x0.75mm, normal (-0.76,-0.65,0), area 6.3mm2, adj f0,f6,f88,f91
  f88: cylinder r=10.8mm len=6.35mm, axis (0,0,-1), area 36.8mm2, adj f0,f6,f87,f89
  f89: cylinder r=3.57mm len=6.35mm, axis (0,0,-1), area 6.8mm2, adj f0,f6,f71,f88
  f90: cylinder r=3.57mm len=6.35mm, axis (0,0,-1), area 6.8mm2, adj f0,f6,f68,f91
  f91: cylinder r=10.8mm len=6.35mm, axis (0,0,-1), area 36.8mm2, adj f0,f6,f87,f90
  f92: plane 6.35x0.92mm, normal (-0.92,-0.39,0), area 6.3mm2, adj f0,f6,f93,f96
  f93: cylinder r=10.8mm len=6.35mm, axis (0,0,-1), area 36.8mm2, adj f0,f6,f92,f94
  f94: cylinder r=3.57mm len=6.35mm, axis (0,0,-1), area 6.8mm2, adj f0,f6,f68,f93
  f95: cylinder r=3.57mm len=6.35mm, axis (0,0,-1), area 6.8mm2, adj f0,f6,f67,f96
  f96: cylinder r=10.8mm len=6.35mm, axis (0,0,-1), area 36.8mm2, adj f0,f6,f92,f95
  f97: plane 6.35x0.99mm, normal (-1,-0.08,0), area 6.3mm2, adj f0,f6,f98,f101
  f98: cylinder r=10.8mm len=6.35mm, axis (0,0,-1), area 36.8mm2, adj f0,f6,f97,f99
  f99: cylinder r=3.57mm len=6.35mm, axis (0,0,-1), area 6.8mm2, adj f0,f6,f67,f98
  f100: cylinder r=3.57mm len=6.35mm, axis (0,0,-1), area 6.8mm2, adj f0,f6,f66,f101
  f101: cylinder r=10.8mm len=6.35mm, axis (0,0,-1), area 36.8mm2, adj f0,f6,f97,f100
  f102: plane 6.35x0.97mm, normal (-0.97,0.23,0), area 6.3mm2, adj f0,f6,f103,f106
  f103: cylinder r=10.8mm len=6.35mm, axis (0,0,-1), area 36.8mm2, adj f0,f6,f102,f104
  f104: cylinder r=3.57mm len=6.35mm, axis (0,0,-1), area 6.8mm2, adj f0,f6,f66,f103
  f105: cylinder r=3.57mm len=6.35mm, axis (0,0,-1), area 6.8mm2, adj f0,f6,f65,f106
  f106: cylinder r=10.8mm len=6.35mm, axis (0,0,-1), area 36.8mm2, adj f0,f6,f102,f105
  f107: plane 6.35x0.85mm, normal (-0.86,0.52,0), area 6.3mm2, adj f0,f6,f108,f111
  f108: cylinder r=10.8mm len=6.35mm, axis (0,0,-1), area 36.8mm2, adj f0,f6,f107,f109
  f109: cylinder r=3.57mm len=6.35mm, axis (0,0,-1), area 6.8mm2, adj f0,f6,f65,f108
  f110: cylinder r=3.57mm len=6.35mm, axis (0,0,-1), area 6.8mm2, adj f0,f6,f64,f111
  f111: cylinder r=10.8mm len=6.35mm, axis (0,0,-1), area 36.8mm2, adj f0,f6,f107,f110
  f112: plane 6.35x0.75mm, normal (-0.65,0.76,0), area 6.3mm2, adj f0,f6,f113,f116
  f113: cylinder r=10.8mm len=6.35mm, axis (0,0,-1), area 36.8mm2, adj f0,f6,f112,f114
  f114: cylinder r=3.57mm len=6.35mm, axis (0,0,-1), area 6.8mm2, adj f0,f6,f64,f113
  f115: cylinder r=3.57mm len=6.35mm, axis (0,0,-1), area 6.8mm2, adj f0,f6,f63,f116
  f116: cylinder r=10.8mm len=6.35mm, axis (0,0,-1), area 36.8mm2, adj f0,f6,f112,f115
  f117: plane 6.35x0.92mm, normal (-0.39,0.92,0), area 6.3mm2, adj f0,f6,f118,f121
  f118: cylinder r=10.8mm len=6.35mm, axis (0,0,-1), area 36.8mm2, adj f0,f6,f117,f119
  f119: cylinder r=3.57mm len=6.35mm, axis (0,0,-1), area 6.8mm2, adj f0,f6,f63,f118
  f120: cylinder r=3.57mm len=6.35mm, axis (0,0,-1), area 6.8mm2, adj f0,f6,f62,f121
  f121: cylinder r=10.8mm len=6.35mm, axis (0,0,-1), area 36.8mm2, adj f0,f6,f117,f120
  f122: cylinder r=3.17mm len=6.35mm, axis (0,0,-1), area 126.7mm2, adj f0,f123
  f123: plane 6.35x6.35mm, normal (0,0,1), area 31.7mm2, adj f122
  f124: cylinder r=3.17mm len=6.35mm, axis (0,0,1), area 126.7mm2, adj f0,f6
PART F: 10 faces, bbox 55.5x12.7x6.4 mm
  f0: plane 42.79x6.35mm, normal (0,-1,0), area 229.8mm2, adj f1,f4,f5,f6,f8,f9
  f1: cylinder r=6.35mm len=12.7mm, axis (0,0,-1), area 126.7mm2, adj f0,f2,f5,f8
  f2: plane 42.79x6.35mm, normal (0,1,0), area 229.8mm2, adj f1,f4,f5,f6,f8,f9
  f3: cylinder r=3.43mm len=6.86mm, axis (0,0,-1), area 136.8mm2, adj f5,f8
  f4: cylinder r=6.35mm len=12.7mm, axis (0,0,-1), area 63.3mm2, adj f0,f2,f5,f9
  f5: plane 42.28x12.7mm, normal (0,0,1), area 465.4mm2, adj f0,f1,f2,f3,f4
  f6: cylinder r=6.35mm len=12.7mm, axis (0,0,1), area 63.3mm2, adj f0,f2,f8,f9
  f7: cylinder r=3.43mm len=6.86mm, axis (0,0,1), area 68.4mm2, adj f8,f9
  f8: plane 55.49x12.7mm, normal (0,0,-1), area 596.2mm2, adj f0,f1,f2,f3,f6,f7
  f9: plane 19.56x12.7mm, normal (0,0,1), area 130.8mm2, adj f0,f2,f4,f6,f7
PLACE A rot(axis=(0,0,-1),51.5deg) t=(-30.02,30.02,0)mm
PLACE B at identity fixed
PLACE C rot(axis=(0,0,-1),5.6deg) t=(-23.75,44.32,0)mm
PLACE D rot(axis=(0,0,-1),10.3deg) t=(47.26,15.96,9.53)mm
PLACE E rot(axis=(0,0,1),171.8deg) t=(83.28,-64.25,0)mm
PLACE F rot(axis=(0,0,-1),67.3deg) t=(21.67,-15.85,9.53)mm
MATE revolute F.f3 <-> E.f7  axis (0,0,-1) through (21.67,-15.85,6.35)mm
MATE revolute D.f5 <-> F.f7  axis (0,0,-1) through (5.16,23.62,9.53)mm
MATE revolute E.f124 <-> B.f6  axis (0,0,1) through (14.88,-14.88,0)mm
MATE revolute C.f9 <-> F.f7  axis (0,0,-1) through (5.16,23.62,6.35)mm
MATE revolute A.f45 <-> D.f4  axis (0,0,1) through (-30.02,30.02,6.35)mm
MATE revolute A.f45 <-> B.f12  axis (0,0,-1) through (-30.02,30.02,0)mm
